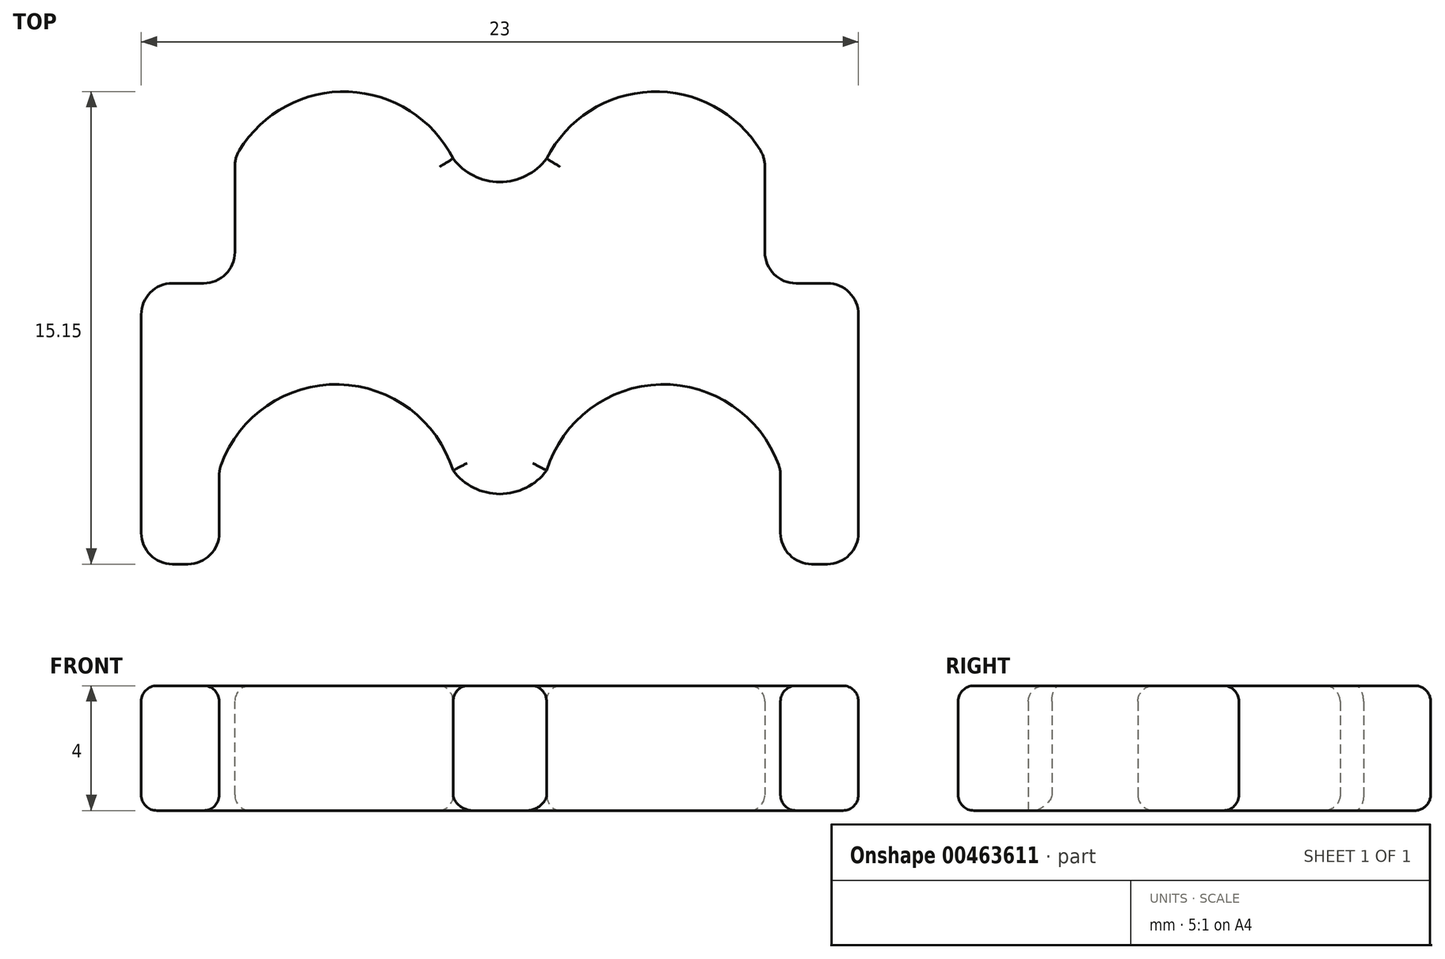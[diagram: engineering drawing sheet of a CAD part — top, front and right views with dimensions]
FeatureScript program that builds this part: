
annotation { "Feature Type Name" : "Feature", "Feature Type Description" : "" }
export const myFeature = defineFeature(function(context is Context, id is Id, definition is map)
    precondition{}
    {
        {
            var Q0;
            Q0=qCreatedBy(makeId("Top.planeOp"),FACE);
            var sketch = newSketch(context, id + "F0", { "sketchPlane" : qUnion([Q0])});
            skLineSegment(sketch, "E0", {"start": v(9, -13) * mm, "end": v(9, -10) * mm});
            skLineSegment(sketch, "E1", {"start": v(-9, -10) * mm, "end": v(-9, -13) * mm});
            skLineSegment(sketch, "E2", {"start": v(-9, -13) * mm, "end": v(-11.5, -13) * mm});
            skLineSegment(sketch, "E3", {"start": v(9, -13) * mm, "end": v(11.5, -13) * mm});
            skLineSegment(sketch, "E4", {"start": v(-11.5, -13) * mm, "end": v(-11.5, -4) * mm});
            skLineSegment(sketch, "E5", {"start": v(-11.5, -4) * mm, "end": v(-8.5, -4) * mm});
            skLineSegment(sketch, "E6", {"start": v(-8.5, -4) * mm, "end": v(-8.5, 0) * mm});
            skLineSegment(sketch, "E7", {"start": v(8.5, 0) * mm, "end": v(8.5, -4) * mm});
            skLineSegment(sketch, "E8", {"start": v(8.5, -4) * mm, "end": v(11.5, -4) * mm});
            skLineSegment(sketch, "E9", {"start": v(11.5, -4) * mm, "end": v(11.5, -13) * mm});
            skArc(sketch, "E10", {"start": v(8.5, 0) * mm, "mid": v(5, 2.15) * mm, "end": v(1.5, 0) * mm});
            skArc(sketch, "E11", {"start": v(-1.5, 0) * mm, "mid": v(0, -0.75) * mm, "end": v(1.5, 0) * mm});
            skArc(sketch, "E12", {"start": v(9, -10) * mm, "mid": v(5.25, -7.24) * mm, "end": v(1.5, -10) * mm});
            skArc(sketch, "E13", {"start": v(-1.5, -10) * mm, "mid": v(0, -10.75) * mm, "end": v(1.5, -10) * mm});
            skArc(sketch, "E14", {"start": v(-1.5, -10) * mm, "mid": v(-5.25, -7.24) * mm, "end": v(-9, -10) * mm});
            skArc(sketch, "E15", {"start": v(-1.5, 0) * mm, "mid": v(-5, 2.15) * mm, "end": v(-8.5, 0) * mm});
            skSolve(sketch);
        }
        {
            var Q0;
            Q0=makeQuery(id+"F0.imprint","IMPRINT",FACE,{"disambiguationData":[TD([[makeQuery(id+"F0.imprint","IMPRINT",EDGE,{"derivedFrom":sQuery(id+"F0.wireOp",EDGE,"E0")}),-1.0]])]});
            extrude(context, id + "F1", {"entities" : qUnion([Q0]), "depth" : 4 * mm});
        }
        {
            var Q0;
            Q0=makeQuery(id+"F1.opExtrude","SWEPT_EDGE",EDGE,{"disambiguationData":[OSD([sQuery(id+"F0.wireOp",EDGE,"JVpa2NSN-jCbz-SYZh-2br0-VPJ9OqO5sEDm"),sQuery(id+"F0.wireOp",EDGE,"TmuEh8Bb-qYGH-lmF9-es9h-PXmLGTj7apYS")])]});
            var Q1;
            Q1=makeQuery(id+"F1.opExtrude","SWEPT_EDGE",EDGE,{"disambiguationData":[OSD([sQuery(id+"F0.wireOp",EDGE,"Ta08JTOG-JjW1-DyQu-Rjfl-olB2hLuTZKrI"),sQuery(id+"F0.wireOp",EDGE,"5RLxsvr7-zWRq-nJ0O-23qe-XEgADmnkmLba")])]});
            var Q2;
            Q2=makeQuery(id+"F1.opExtrude","SWEPT_EDGE",EDGE,{"disambiguationData":[OSD([sQuery(id+"F0.wireOp",EDGE,"JVpa2NSN-jCbz-SYZh-2br0-VPJ9OqO5sEDm"),sQuery(id+"F0.wireOp",EDGE,"iIMMWLLX-5pRk-kAWc-YyXh-X3XYjQtiHgF8")])]});
            var Q3;
            Q3=makeQuery(id+"F1.opExtrude","SWEPT_EDGE",EDGE,{"disambiguationData":[OSD([sQuery(id+"F0.wireOp",EDGE,"Bp2VUUx9-f2Nf-Cqm2-FavC-f2X54JljXIIN"),sQuery(id+"F0.wireOp",EDGE,"TmuEh8Bb-qYGH-lmF9-es9h-PXmLGTj7apYS")])]});
            var Q4;
            Q4=makeQuery(id+"F1.opExtrude","SWEPT_EDGE",EDGE,{"disambiguationData":[OSD([sQuery(id+"F0.wireOp",EDGE,"aM0JYdi9-BpOH-c1Sx-eQZ7-4LdQcpM627Qa"),sQuery(id+"F0.wireOp",EDGE,"Ta08JTOG-JjW1-DyQu-Rjfl-olB2hLuTZKrI")])]});
            var Q5;
            Q5=makeQuery(id+"F1.opExtrude","SWEPT_EDGE",EDGE,{"disambiguationData":[OSD([sQuery(id+"F0.wireOp",EDGE,"5RLxsvr7-zWRq-nJ0O-23qe-XEgADmnkmLba"),sQuery(id+"F0.wireOp",EDGE,"Bp2VUUx9-f2Nf-Cqm2-FavC-f2X54JljXIIN")])]});
            var Q6;
            Q6=makeQuery(id+"F1.opExtrude","SWEPT_EDGE",EDGE,{"disambiguationData":[OSD([sQuery(id+"F0.wireOp",EDGE,"yeDMJLls-6pq1-5wso-vwFU-Q73Pk40JU32b"),sQuery(id+"F0.wireOp",EDGE,"aM0JYdi9-BpOH-c1Sx-eQZ7-4LdQcpM627Qa")])]});
            var Q7;
            Q7=makeQuery(id+"F1.opExtrude","SWEPT_EDGE",EDGE,{"disambiguationData":[OSD([sQuery(id+"F0.wireOp",EDGE,"yeDMJLls-6pq1-5wso-vwFU-Q73Pk40JU32b"),sQuery(id+"F0.wireOp",EDGE,"oADVPvip-QRiO-k2je-1GcM-0gCGYZzCVpqe")])]});
            var Q8;
            Q8=makeQuery(id+"F1.opExtrude","SWEPT_EDGE",EDGE,{"disambiguationData":[OSD([sQuery(id+"F0.wireOp",EDGE,"oADVPvip-QRiO-k2je-1GcM-0gCGYZzCVpqe"),sQuery(id+"F0.wireOp",EDGE,"10rlgXVg-n50c-kqx7-uExC-2RYqwfv1c7cX")])]});
            var Q9;
            Q9=makeQuery(id+"F1.opExtrude","SWEPT_EDGE",EDGE,{"disambiguationData":[OSD([sQuery(id+"F0.wireOp",EDGE,"TUznSBm0-cCe5-ovrQ-pSbA-vPagOil4q95r"),sQuery(id+"F0.wireOp",EDGE,"10rlgXVg-n50c-kqx7-uExC-2RYqwfv1c7cX")])]});
            var Q10;
            Q10=makeQuery(id+"F1.opExtrude","SWEPT_EDGE",EDGE,{"disambiguationData":[OSD([sQuery(id+"F0.wireOp",EDGE,"dIuJsfEi-w8Eu-UMFV-xWrQ-Q2fZL97E1xqK"),sQuery(id+"F0.wireOp",EDGE,"TUznSBm0-cCe5-ovrQ-pSbA-vPagOil4q95r")])]});
            var Q11;
            Q11=makeQuery(id+"F1.opExtrude","SWEPT_EDGE",EDGE,{"disambiguationData":[OSD([sQuery(id+"F0.wireOp",EDGE,"iIMMWLLX-5pRk-kAWc-YyXh-X3XYjQtiHgF8"),sQuery(id+"F0.wireOp",EDGE,"dIuJsfEi-w8Eu-UMFV-xWrQ-Q2fZL97E1xqK")])]});
            var Q12;
            Q12=makeQuery(id+"F1.opExtrude","SWEPT_EDGE",EDGE,{"disambiguationData":[OSD([sQuery(id+"F0.wireOp",EDGE,"yLF3BCVI-Jb2U-5dZP-aiB0-7200LCA53yiJ"),sQuery(id+"F0.wireOp",EDGE,"E2")])]});
            var Q13;
            Q13=makeQuery(id+"F1.opExtrude","SWEPT_EDGE",EDGE,{"disambiguationData":[OSD([sQuery(id+"F0.wireOp",EDGE,"E1"),sQuery(id+"F0.wireOp",EDGE,"E2")])]});
            var Q14;
            Q14=makeQuery(id+"F1.opExtrude","SWEPT_EDGE",EDGE,{"disambiguationData":[OSD([sQuery(id+"F0.wireOp",EDGE,"Zq1giByw-Wy4a-OScs-KzMb-DU4RaiEdW2Sl"),sQuery(id+"F0.wireOp",EDGE,"E1")])]});
            var Q15;
            Q15=makeQuery(id+"F1.opExtrude","SWEPT_EDGE",EDGE,{"disambiguationData":[OSD([sQuery(id+"F0.wireOp",EDGE,"E0"),sQuery(id+"F0.wireOp",EDGE,"Zq1giByw-Wy4a-OScs-KzMb-DU4RaiEdW2Sl")])]});
            var Q16;
            Q16=makeQuery(id+"F1.opExtrude","SWEPT_EDGE",EDGE,{"disambiguationData":[OSD([sQuery(id+"F0.wireOp",EDGE,"E0"),sQuery(id+"F0.wireOp",EDGE,"E3")])]});
            var Q17;
            Q17=makeQuery(id+"F1.opExtrude","SWEPT_EDGE",EDGE,{"disambiguationData":[OSD([sQuery(id+"F0.wireOp",EDGE,"W0sLsfjq-YAJu-qSV0-cM3q-n6XLMPe2tytr"),sQuery(id+"F0.wireOp",EDGE,"E3")])]});
            var Q18;
            Q18=makeQuery(id+"F1.opExtrude","SWEPT_EDGE",EDGE,{"disambiguationData":[OSD([sQuery(id+"F0.wireOp",EDGE,"E4"),sQuery(id+"F0.wireOp",EDGE,"E5")])]});
            var Q19;
            Q19=makeQuery(id+"F1.opExtrude","SWEPT_EDGE",EDGE,{"disambiguationData":[OSD([sQuery(id+"F0.wireOp",EDGE,"E5"),sQuery(id+"F0.wireOp",EDGE,"E6")])]});
            var Q20;
            Q20=makeQuery(id+"F1.opExtrude","SWEPT_EDGE",EDGE,{"disambiguationData":[OSD([sQuery(id+"F0.wireOp",EDGE,"E6"),sQuery(id+"F0.wireOp",EDGE,"37HIgoPE-k505-ApNl-kPiv-Fzmli7TXVLkK")])]});
            var Q21;
            Q21=makeQuery(id+"F1.opExtrude","SWEPT_EDGE",EDGE,{"disambiguationData":[OSD([sQuery(id+"F0.wireOp",EDGE,"37HIgoPE-k505-ApNl-kPiv-Fzmli7TXVLkK"),sQuery(id+"F0.wireOp",EDGE,"E7")])]});
            var Q22;
            Q22=makeQuery(id+"F1.opExtrude","SWEPT_EDGE",EDGE,{"disambiguationData":[OSD([sQuery(id+"F0.wireOp",EDGE,"E7"),sQuery(id+"F0.wireOp",EDGE,"E8")])]});
            var Q23;
            Q23=makeQuery(id+"F1.opExtrude","SWEPT_EDGE",EDGE,{"disambiguationData":[OSD([sQuery(id+"F0.wireOp",EDGE,"E8"),sQuery(id+"F0.wireOp",EDGE,"E9")])]});
            fillet(context, id + "F2", {"entities" : qUnion([Q0, Q1, Q2, Q3, Q4, Q5, Q6, Q7, Q8, Q9, Q10, Q11, Q12, Q13, Q14, Q15, Q16, Q17, Q18, Q19, Q20, Q21, Q22, Q23]), "radius" : 1 * mm, "tangentPropagation" : true, "allowEdgeOverflow" : false});
        }
        {
            var Q0;
            Q0=makeQuery(id+"F1.opExtrude","CAP_EDGE",EDGE,{"disambiguationData":[OSD([sQuery(id+"F0.wireOp",EDGE,"E15")])],"isStart":false});
            var Q1;
            {var subQ0=sQuery(id+"F0.wireOp",EDGE,"E15");var subQ1=sQuery(id+"F0.wireOp",EDGE,"E6");Q1=makeQuery(id+"F2.opFillet","BLEND_EDGE",EDGE,{"blendedFrom":[makeQuery(id+"F1.opExtrude","SWEPT_EDGE",EDGE,{"disambiguationData":[OSD([subQ1,subQ0])]}),makeQuery(id+"F1.opExtrude","CAP_FACE",FACE,{"disambiguationData":[OSD([sQuery(id+"F0.wireOp",EDGE,"E0"),sQuery(id+"F0.wireOp",EDGE,"E1"),sQuery(id+"F0.wireOp",EDGE,"E2"),sQuery(id+"F0.wireOp",EDGE,"E3"),sQuery(id+"F0.wireOp",EDGE,"E4"),sQuery(id+"F0.wireOp",EDGE,"E5"),subQ1,sQuery(id+"F0.wireOp",EDGE,"E7"),sQuery(id+"F0.wireOp",EDGE,"E8"),sQuery(id+"F0.wireOp",EDGE,"E9"),sQuery(id+"F0.wireOp",EDGE,"E10"),sQuery(id+"F0.wireOp",EDGE,"E11"),sQuery(id+"F0.wireOp",EDGE,"E12"),sQuery(id+"F0.wireOp",EDGE,"E13"),sQuery(id+"F0.wireOp",EDGE,"E14"),subQ0])],"isStart":false})],"blendedInto":[makeQuery(id+"F1.opExtrude","CAP_FACE",FACE,{"disambiguationData":[OSD([sQuery(id+"F0.wireOp",EDGE,"E0"),sQuery(id+"F0.wireOp",EDGE,"E1"),sQuery(id+"F0.wireOp",EDGE,"E2"),sQuery(id+"F0.wireOp",EDGE,"E3"),sQuery(id+"F0.wireOp",EDGE,"E4"),sQuery(id+"F0.wireOp",EDGE,"E5"),subQ1,sQuery(id+"F0.wireOp",EDGE,"E7"),sQuery(id+"F0.wireOp",EDGE,"E8"),sQuery(id+"F0.wireOp",EDGE,"E9"),sQuery(id+"F0.wireOp",EDGE,"E10"),sQuery(id+"F0.wireOp",EDGE,"E11"),sQuery(id+"F0.wireOp",EDGE,"E12"),sQuery(id+"F0.wireOp",EDGE,"E13"),sQuery(id+"F0.wireOp",EDGE,"E14"),subQ0])],"isStart":false})]});}
            var Q2;
            Q2=makeQuery(id+"F1.opExtrude","CAP_EDGE",EDGE,{"disambiguationData":[OSD([sQuery(id+"F0.wireOp",EDGE,"E6")])],"isStart":false});
            var Q3;
            {var subQ0=sQuery(id+"F0.wireOp",EDGE,"E6");var subQ1=sQuery(id+"F0.wireOp",EDGE,"E5");Q3=makeQuery(id+"F2.opFillet","BLEND_EDGE",EDGE,{"blendedFrom":[makeQuery(id+"F1.opExtrude","SWEPT_EDGE",EDGE,{"disambiguationData":[OSD([subQ1,subQ0])]}),makeQuery(id+"F1.opExtrude","CAP_FACE",FACE,{"disambiguationData":[OSD([sQuery(id+"F0.wireOp",EDGE,"E0"),sQuery(id+"F0.wireOp",EDGE,"E1"),sQuery(id+"F0.wireOp",EDGE,"E2"),sQuery(id+"F0.wireOp",EDGE,"E3"),sQuery(id+"F0.wireOp",EDGE,"E4"),subQ1,subQ0,sQuery(id+"F0.wireOp",EDGE,"E7"),sQuery(id+"F0.wireOp",EDGE,"E8"),sQuery(id+"F0.wireOp",EDGE,"E9"),sQuery(id+"F0.wireOp",EDGE,"E10"),sQuery(id+"F0.wireOp",EDGE,"E11"),sQuery(id+"F0.wireOp",EDGE,"E12"),sQuery(id+"F0.wireOp",EDGE,"E13"),sQuery(id+"F0.wireOp",EDGE,"E14"),sQuery(id+"F0.wireOp",EDGE,"E15")])],"isStart":false})],"blendedInto":[makeQuery(id+"F1.opExtrude","CAP_FACE",FACE,{"disambiguationData":[OSD([sQuery(id+"F0.wireOp",EDGE,"E0"),sQuery(id+"F0.wireOp",EDGE,"E1"),sQuery(id+"F0.wireOp",EDGE,"E2"),sQuery(id+"F0.wireOp",EDGE,"E3"),sQuery(id+"F0.wireOp",EDGE,"E4"),subQ1,subQ0,sQuery(id+"F0.wireOp",EDGE,"E7"),sQuery(id+"F0.wireOp",EDGE,"E8"),sQuery(id+"F0.wireOp",EDGE,"E9"),sQuery(id+"F0.wireOp",EDGE,"E10"),sQuery(id+"F0.wireOp",EDGE,"E11"),sQuery(id+"F0.wireOp",EDGE,"E12"),sQuery(id+"F0.wireOp",EDGE,"E13"),sQuery(id+"F0.wireOp",EDGE,"E14"),sQuery(id+"F0.wireOp",EDGE,"E15")])],"isStart":false})]});}
            var Q4;
            Q4=makeQuery(id+"F1.opExtrude","CAP_EDGE",EDGE,{"disambiguationData":[OSD([sQuery(id+"F0.wireOp",EDGE,"E5")])],"isStart":false});
            var Q5;
            {var subQ0=sQuery(id+"F0.wireOp",EDGE,"E5");var subQ1=sQuery(id+"F0.wireOp",EDGE,"E4");Q5=makeQuery(id+"F2.opFillet","BLEND_EDGE",EDGE,{"blendedFrom":[makeQuery(id+"F1.opExtrude","SWEPT_EDGE",EDGE,{"disambiguationData":[OSD([subQ1,subQ0])]}),makeQuery(id+"F1.opExtrude","CAP_FACE",FACE,{"disambiguationData":[OSD([sQuery(id+"F0.wireOp",EDGE,"E0"),sQuery(id+"F0.wireOp",EDGE,"E1"),sQuery(id+"F0.wireOp",EDGE,"E2"),sQuery(id+"F0.wireOp",EDGE,"E3"),subQ1,subQ0,sQuery(id+"F0.wireOp",EDGE,"E6"),sQuery(id+"F0.wireOp",EDGE,"E7"),sQuery(id+"F0.wireOp",EDGE,"E8"),sQuery(id+"F0.wireOp",EDGE,"E9"),sQuery(id+"F0.wireOp",EDGE,"E10"),sQuery(id+"F0.wireOp",EDGE,"E11"),sQuery(id+"F0.wireOp",EDGE,"E12"),sQuery(id+"F0.wireOp",EDGE,"E13"),sQuery(id+"F0.wireOp",EDGE,"E14"),sQuery(id+"F0.wireOp",EDGE,"E15")])],"isStart":false})],"blendedInto":[makeQuery(id+"F1.opExtrude","CAP_FACE",FACE,{"disambiguationData":[OSD([sQuery(id+"F0.wireOp",EDGE,"E0"),sQuery(id+"F0.wireOp",EDGE,"E1"),sQuery(id+"F0.wireOp",EDGE,"E2"),sQuery(id+"F0.wireOp",EDGE,"E3"),subQ1,subQ0,sQuery(id+"F0.wireOp",EDGE,"E6"),sQuery(id+"F0.wireOp",EDGE,"E7"),sQuery(id+"F0.wireOp",EDGE,"E8"),sQuery(id+"F0.wireOp",EDGE,"E9"),sQuery(id+"F0.wireOp",EDGE,"E10"),sQuery(id+"F0.wireOp",EDGE,"E11"),sQuery(id+"F0.wireOp",EDGE,"E12"),sQuery(id+"F0.wireOp",EDGE,"E13"),sQuery(id+"F0.wireOp",EDGE,"E14"),sQuery(id+"F0.wireOp",EDGE,"E15")])],"isStart":false})]});}
            var Q6;
            Q6=makeQuery(id+"F1.opExtrude","CAP_EDGE",EDGE,{"disambiguationData":[OSD([sQuery(id+"F0.wireOp",EDGE,"E4")])],"isStart":false});
            var Q7;
            {var subQ0=sQuery(id+"F0.wireOp",EDGE,"E4");var subQ1=sQuery(id+"F0.wireOp",EDGE,"E2");Q7=makeQuery(id+"F2.opFillet","BLEND_EDGE",EDGE,{"blendedFrom":[makeQuery(id+"F1.opExtrude","SWEPT_EDGE",EDGE,{"disambiguationData":[OSD([subQ1,subQ0])]}),makeQuery(id+"F1.opExtrude","CAP_FACE",FACE,{"disambiguationData":[OSD([sQuery(id+"F0.wireOp",EDGE,"E0"),sQuery(id+"F0.wireOp",EDGE,"E1"),subQ1,sQuery(id+"F0.wireOp",EDGE,"E3"),subQ0,sQuery(id+"F0.wireOp",EDGE,"E5"),sQuery(id+"F0.wireOp",EDGE,"E6"),sQuery(id+"F0.wireOp",EDGE,"E7"),sQuery(id+"F0.wireOp",EDGE,"E8"),sQuery(id+"F0.wireOp",EDGE,"E9"),sQuery(id+"F0.wireOp",EDGE,"E10"),sQuery(id+"F0.wireOp",EDGE,"E11"),sQuery(id+"F0.wireOp",EDGE,"E12"),sQuery(id+"F0.wireOp",EDGE,"E13"),sQuery(id+"F0.wireOp",EDGE,"E14"),sQuery(id+"F0.wireOp",EDGE,"E15")])],"isStart":false})],"blendedInto":[makeQuery(id+"F1.opExtrude","CAP_FACE",FACE,{"disambiguationData":[OSD([sQuery(id+"F0.wireOp",EDGE,"E0"),sQuery(id+"F0.wireOp",EDGE,"E1"),subQ1,sQuery(id+"F0.wireOp",EDGE,"E3"),subQ0,sQuery(id+"F0.wireOp",EDGE,"E5"),sQuery(id+"F0.wireOp",EDGE,"E6"),sQuery(id+"F0.wireOp",EDGE,"E7"),sQuery(id+"F0.wireOp",EDGE,"E8"),sQuery(id+"F0.wireOp",EDGE,"E9"),sQuery(id+"F0.wireOp",EDGE,"E10"),sQuery(id+"F0.wireOp",EDGE,"E11"),sQuery(id+"F0.wireOp",EDGE,"E12"),sQuery(id+"F0.wireOp",EDGE,"E13"),sQuery(id+"F0.wireOp",EDGE,"E14"),sQuery(id+"F0.wireOp",EDGE,"E15")])],"isStart":false})]});}
            var Q8;
            Q8=makeQuery(id+"F1.opExtrude","CAP_EDGE",EDGE,{"disambiguationData":[OSD([sQuery(id+"F0.wireOp",EDGE,"E2")])],"isStart":false});
            var Q9;
            {var subQ0=sQuery(id+"F0.wireOp",EDGE,"E2");var subQ1=sQuery(id+"F0.wireOp",EDGE,"E1");Q9=makeQuery(id+"F2.opFillet","BLEND_EDGE",EDGE,{"blendedFrom":[makeQuery(id+"F1.opExtrude","SWEPT_EDGE",EDGE,{"disambiguationData":[OSD([subQ1,subQ0])]}),makeQuery(id+"F1.opExtrude","CAP_FACE",FACE,{"disambiguationData":[OSD([sQuery(id+"F0.wireOp",EDGE,"E0"),subQ1,subQ0,sQuery(id+"F0.wireOp",EDGE,"E3"),sQuery(id+"F0.wireOp",EDGE,"E4"),sQuery(id+"F0.wireOp",EDGE,"E5"),sQuery(id+"F0.wireOp",EDGE,"E6"),sQuery(id+"F0.wireOp",EDGE,"E7"),sQuery(id+"F0.wireOp",EDGE,"E8"),sQuery(id+"F0.wireOp",EDGE,"E9"),sQuery(id+"F0.wireOp",EDGE,"E10"),sQuery(id+"F0.wireOp",EDGE,"E11"),sQuery(id+"F0.wireOp",EDGE,"E12"),sQuery(id+"F0.wireOp",EDGE,"E13"),sQuery(id+"F0.wireOp",EDGE,"E14"),sQuery(id+"F0.wireOp",EDGE,"E15")])],"isStart":false})],"blendedInto":[makeQuery(id+"F1.opExtrude","CAP_FACE",FACE,{"disambiguationData":[OSD([sQuery(id+"F0.wireOp",EDGE,"E0"),subQ1,subQ0,sQuery(id+"F0.wireOp",EDGE,"E3"),sQuery(id+"F0.wireOp",EDGE,"E4"),sQuery(id+"F0.wireOp",EDGE,"E5"),sQuery(id+"F0.wireOp",EDGE,"E6"),sQuery(id+"F0.wireOp",EDGE,"E7"),sQuery(id+"F0.wireOp",EDGE,"E8"),sQuery(id+"F0.wireOp",EDGE,"E9"),sQuery(id+"F0.wireOp",EDGE,"E10"),sQuery(id+"F0.wireOp",EDGE,"E11"),sQuery(id+"F0.wireOp",EDGE,"E12"),sQuery(id+"F0.wireOp",EDGE,"E13"),sQuery(id+"F0.wireOp",EDGE,"E14"),sQuery(id+"F0.wireOp",EDGE,"E15")])],"isStart":false})]});}
            var Q10;
            Q10=makeQuery(id+"F1.opExtrude","CAP_EDGE",EDGE,{"disambiguationData":[OSD([sQuery(id+"F0.wireOp",EDGE,"E1")])],"isStart":false});
            var Q11;
            Q11=makeQuery(id+"F1.opExtrude","CAP_EDGE",EDGE,{"disambiguationData":[OSD([sQuery(id+"F0.wireOp",EDGE,"E14")])],"isStart":false});
            var Q12;
            {var subQ0=sQuery(id+"F0.wireOp",EDGE,"E14");var subQ1=sQuery(id+"F0.wireOp",EDGE,"E1");Q12=makeQuery(id+"F2.opFillet","BLEND_EDGE",EDGE,{"blendedFrom":[makeQuery(id+"F1.opExtrude","SWEPT_EDGE",EDGE,{"disambiguationData":[OSD([subQ1,subQ0])]}),makeQuery(id+"F1.opExtrude","CAP_FACE",FACE,{"disambiguationData":[OSD([sQuery(id+"F0.wireOp",EDGE,"E0"),subQ1,sQuery(id+"F0.wireOp",EDGE,"E2"),sQuery(id+"F0.wireOp",EDGE,"E3"),sQuery(id+"F0.wireOp",EDGE,"E4"),sQuery(id+"F0.wireOp",EDGE,"E5"),sQuery(id+"F0.wireOp",EDGE,"E6"),sQuery(id+"F0.wireOp",EDGE,"E7"),sQuery(id+"F0.wireOp",EDGE,"E8"),sQuery(id+"F0.wireOp",EDGE,"E9"),sQuery(id+"F0.wireOp",EDGE,"E10"),sQuery(id+"F0.wireOp",EDGE,"E11"),sQuery(id+"F0.wireOp",EDGE,"E12"),sQuery(id+"F0.wireOp",EDGE,"E13"),subQ0,sQuery(id+"F0.wireOp",EDGE,"E15")])],"isStart":false})],"blendedInto":[makeQuery(id+"F1.opExtrude","CAP_FACE",FACE,{"disambiguationData":[OSD([sQuery(id+"F0.wireOp",EDGE,"E0"),subQ1,sQuery(id+"F0.wireOp",EDGE,"E2"),sQuery(id+"F0.wireOp",EDGE,"E3"),sQuery(id+"F0.wireOp",EDGE,"E4"),sQuery(id+"F0.wireOp",EDGE,"E5"),sQuery(id+"F0.wireOp",EDGE,"E6"),sQuery(id+"F0.wireOp",EDGE,"E7"),sQuery(id+"F0.wireOp",EDGE,"E8"),sQuery(id+"F0.wireOp",EDGE,"E9"),sQuery(id+"F0.wireOp",EDGE,"E10"),sQuery(id+"F0.wireOp",EDGE,"E11"),sQuery(id+"F0.wireOp",EDGE,"E12"),sQuery(id+"F0.wireOp",EDGE,"E13"),subQ0,sQuery(id+"F0.wireOp",EDGE,"E15")])],"isStart":false})]});}
            var Q13;
            Q13=makeQuery(id+"F1.opExtrude","CAP_EDGE",EDGE,{"disambiguationData":[OSD([sQuery(id+"F0.wireOp",EDGE,"E13")])],"isStart":false});
            var Q14;
            Q14=makeQuery(id+"F1.opExtrude","CAP_EDGE",EDGE,{"disambiguationData":[OSD([sQuery(id+"F0.wireOp",EDGE,"E12")])],"isStart":false});
            var Q15;
            {var subQ0=sQuery(id+"F0.wireOp",EDGE,"E12");var subQ1=sQuery(id+"F0.wireOp",EDGE,"E0");Q15=makeQuery(id+"F2.opFillet","BLEND_EDGE",EDGE,{"blendedFrom":[makeQuery(id+"F1.opExtrude","SWEPT_EDGE",EDGE,{"disambiguationData":[OSD([subQ1,subQ0])]}),makeQuery(id+"F1.opExtrude","CAP_FACE",FACE,{"disambiguationData":[OSD([subQ1,sQuery(id+"F0.wireOp",EDGE,"E1"),sQuery(id+"F0.wireOp",EDGE,"E2"),sQuery(id+"F0.wireOp",EDGE,"E3"),sQuery(id+"F0.wireOp",EDGE,"E4"),sQuery(id+"F0.wireOp",EDGE,"E5"),sQuery(id+"F0.wireOp",EDGE,"E6"),sQuery(id+"F0.wireOp",EDGE,"E7"),sQuery(id+"F0.wireOp",EDGE,"E8"),sQuery(id+"F0.wireOp",EDGE,"E9"),sQuery(id+"F0.wireOp",EDGE,"E10"),sQuery(id+"F0.wireOp",EDGE,"E11"),subQ0,sQuery(id+"F0.wireOp",EDGE,"E13"),sQuery(id+"F0.wireOp",EDGE,"E14"),sQuery(id+"F0.wireOp",EDGE,"E15")])],"isStart":false})],"blendedInto":[makeQuery(id+"F1.opExtrude","CAP_FACE",FACE,{"disambiguationData":[OSD([subQ1,sQuery(id+"F0.wireOp",EDGE,"E1"),sQuery(id+"F0.wireOp",EDGE,"E2"),sQuery(id+"F0.wireOp",EDGE,"E3"),sQuery(id+"F0.wireOp",EDGE,"E4"),sQuery(id+"F0.wireOp",EDGE,"E5"),sQuery(id+"F0.wireOp",EDGE,"E6"),sQuery(id+"F0.wireOp",EDGE,"E7"),sQuery(id+"F0.wireOp",EDGE,"E8"),sQuery(id+"F0.wireOp",EDGE,"E9"),sQuery(id+"F0.wireOp",EDGE,"E10"),sQuery(id+"F0.wireOp",EDGE,"E11"),subQ0,sQuery(id+"F0.wireOp",EDGE,"E13"),sQuery(id+"F0.wireOp",EDGE,"E14"),sQuery(id+"F0.wireOp",EDGE,"E15")])],"isStart":false})]});}
            var Q16;
            Q16=makeQuery(id+"F1.opExtrude","CAP_EDGE",EDGE,{"disambiguationData":[OSD([sQuery(id+"F0.wireOp",EDGE,"E0")])],"isStart":false});
            var Q17;
            {var subQ0=sQuery(id+"F0.wireOp",EDGE,"E3");var subQ1=sQuery(id+"F0.wireOp",EDGE,"E0");Q17=makeQuery(id+"F2.opFillet","BLEND_EDGE",EDGE,{"blendedFrom":[makeQuery(id+"F1.opExtrude","SWEPT_EDGE",EDGE,{"disambiguationData":[OSD([subQ1,subQ0])]}),makeQuery(id+"F1.opExtrude","CAP_FACE",FACE,{"disambiguationData":[OSD([subQ1,sQuery(id+"F0.wireOp",EDGE,"E1"),sQuery(id+"F0.wireOp",EDGE,"E2"),subQ0,sQuery(id+"F0.wireOp",EDGE,"E4"),sQuery(id+"F0.wireOp",EDGE,"E5"),sQuery(id+"F0.wireOp",EDGE,"E6"),sQuery(id+"F0.wireOp",EDGE,"E7"),sQuery(id+"F0.wireOp",EDGE,"E8"),sQuery(id+"F0.wireOp",EDGE,"E9"),sQuery(id+"F0.wireOp",EDGE,"E10"),sQuery(id+"F0.wireOp",EDGE,"E11"),sQuery(id+"F0.wireOp",EDGE,"E12"),sQuery(id+"F0.wireOp",EDGE,"E13"),sQuery(id+"F0.wireOp",EDGE,"E14"),sQuery(id+"F0.wireOp",EDGE,"E15")])],"isStart":false})],"blendedInto":[makeQuery(id+"F1.opExtrude","CAP_FACE",FACE,{"disambiguationData":[OSD([subQ1,sQuery(id+"F0.wireOp",EDGE,"E1"),sQuery(id+"F0.wireOp",EDGE,"E2"),subQ0,sQuery(id+"F0.wireOp",EDGE,"E4"),sQuery(id+"F0.wireOp",EDGE,"E5"),sQuery(id+"F0.wireOp",EDGE,"E6"),sQuery(id+"F0.wireOp",EDGE,"E7"),sQuery(id+"F0.wireOp",EDGE,"E8"),sQuery(id+"F0.wireOp",EDGE,"E9"),sQuery(id+"F0.wireOp",EDGE,"E10"),sQuery(id+"F0.wireOp",EDGE,"E11"),sQuery(id+"F0.wireOp",EDGE,"E12"),sQuery(id+"F0.wireOp",EDGE,"E13"),sQuery(id+"F0.wireOp",EDGE,"E14"),sQuery(id+"F0.wireOp",EDGE,"E15")])],"isStart":false})]});}
            var Q18;
            Q18=makeQuery(id+"F1.opExtrude","CAP_EDGE",EDGE,{"disambiguationData":[OSD([sQuery(id+"F0.wireOp",EDGE,"E3")])],"isStart":false});
            var Q19;
            {var subQ0=sQuery(id+"F0.wireOp",EDGE,"E9");var subQ1=sQuery(id+"F0.wireOp",EDGE,"E3");Q19=makeQuery(id+"F2.opFillet","BLEND_EDGE",EDGE,{"blendedFrom":[makeQuery(id+"F1.opExtrude","SWEPT_EDGE",EDGE,{"disambiguationData":[OSD([subQ1,subQ0])]}),makeQuery(id+"F1.opExtrude","CAP_FACE",FACE,{"disambiguationData":[OSD([sQuery(id+"F0.wireOp",EDGE,"E0"),sQuery(id+"F0.wireOp",EDGE,"E1"),sQuery(id+"F0.wireOp",EDGE,"E2"),subQ1,sQuery(id+"F0.wireOp",EDGE,"E4"),sQuery(id+"F0.wireOp",EDGE,"E5"),sQuery(id+"F0.wireOp",EDGE,"E6"),sQuery(id+"F0.wireOp",EDGE,"E7"),sQuery(id+"F0.wireOp",EDGE,"E8"),subQ0,sQuery(id+"F0.wireOp",EDGE,"E10"),sQuery(id+"F0.wireOp",EDGE,"E11"),sQuery(id+"F0.wireOp",EDGE,"E12"),sQuery(id+"F0.wireOp",EDGE,"E13"),sQuery(id+"F0.wireOp",EDGE,"E14"),sQuery(id+"F0.wireOp",EDGE,"E15")])],"isStart":false})],"blendedInto":[makeQuery(id+"F1.opExtrude","CAP_FACE",FACE,{"disambiguationData":[OSD([sQuery(id+"F0.wireOp",EDGE,"E0"),sQuery(id+"F0.wireOp",EDGE,"E1"),sQuery(id+"F0.wireOp",EDGE,"E2"),subQ1,sQuery(id+"F0.wireOp",EDGE,"E4"),sQuery(id+"F0.wireOp",EDGE,"E5"),sQuery(id+"F0.wireOp",EDGE,"E6"),sQuery(id+"F0.wireOp",EDGE,"E7"),sQuery(id+"F0.wireOp",EDGE,"E8"),subQ0,sQuery(id+"F0.wireOp",EDGE,"E10"),sQuery(id+"F0.wireOp",EDGE,"E11"),sQuery(id+"F0.wireOp",EDGE,"E12"),sQuery(id+"F0.wireOp",EDGE,"E13"),sQuery(id+"F0.wireOp",EDGE,"E14"),sQuery(id+"F0.wireOp",EDGE,"E15")])],"isStart":false})]});}
            var Q20;
            Q20=makeQuery(id+"F1.opExtrude","CAP_EDGE",EDGE,{"disambiguationData":[OSD([sQuery(id+"F0.wireOp",EDGE,"E9")])],"isStart":false});
            var Q21;
            Q21=makeQuery(id+"F1.opExtrude","CAP_EDGE",EDGE,{"disambiguationData":[OSD([sQuery(id+"F0.wireOp",EDGE,"E8")])],"isStart":false});
            var Q22;
            {var subQ0=sQuery(id+"F0.wireOp",EDGE,"E8");var subQ1=sQuery(id+"F0.wireOp",EDGE,"E7");Q22=makeQuery(id+"F2.opFillet","BLEND_EDGE",EDGE,{"blendedFrom":[makeQuery(id+"F1.opExtrude","SWEPT_EDGE",EDGE,{"disambiguationData":[OSD([subQ1,subQ0])]}),makeQuery(id+"F1.opExtrude","CAP_FACE",FACE,{"disambiguationData":[OSD([sQuery(id+"F0.wireOp",EDGE,"E0"),sQuery(id+"F0.wireOp",EDGE,"E1"),sQuery(id+"F0.wireOp",EDGE,"E2"),sQuery(id+"F0.wireOp",EDGE,"E3"),sQuery(id+"F0.wireOp",EDGE,"E4"),sQuery(id+"F0.wireOp",EDGE,"E5"),sQuery(id+"F0.wireOp",EDGE,"E6"),subQ1,subQ0,sQuery(id+"F0.wireOp",EDGE,"E9"),sQuery(id+"F0.wireOp",EDGE,"E10"),sQuery(id+"F0.wireOp",EDGE,"E11"),sQuery(id+"F0.wireOp",EDGE,"E12"),sQuery(id+"F0.wireOp",EDGE,"E13"),sQuery(id+"F0.wireOp",EDGE,"E14"),sQuery(id+"F0.wireOp",EDGE,"E15")])],"isStart":false})],"blendedInto":[makeQuery(id+"F1.opExtrude","CAP_FACE",FACE,{"disambiguationData":[OSD([sQuery(id+"F0.wireOp",EDGE,"E0"),sQuery(id+"F0.wireOp",EDGE,"E1"),sQuery(id+"F0.wireOp",EDGE,"E2"),sQuery(id+"F0.wireOp",EDGE,"E3"),sQuery(id+"F0.wireOp",EDGE,"E4"),sQuery(id+"F0.wireOp",EDGE,"E5"),sQuery(id+"F0.wireOp",EDGE,"E6"),subQ1,subQ0,sQuery(id+"F0.wireOp",EDGE,"E9"),sQuery(id+"F0.wireOp",EDGE,"E10"),sQuery(id+"F0.wireOp",EDGE,"E11"),sQuery(id+"F0.wireOp",EDGE,"E12"),sQuery(id+"F0.wireOp",EDGE,"E13"),sQuery(id+"F0.wireOp",EDGE,"E14"),sQuery(id+"F0.wireOp",EDGE,"E15")])],"isStart":false})]});}
            var Q23;
            {var subQ0=sQuery(id+"F0.wireOp",EDGE,"E9");var subQ1=sQuery(id+"F0.wireOp",EDGE,"E8");Q23=makeQuery(id+"F2.opFillet","BLEND_EDGE",EDGE,{"blendedFrom":[makeQuery(id+"F1.opExtrude","SWEPT_EDGE",EDGE,{"disambiguationData":[OSD([subQ1,subQ0])]}),makeQuery(id+"F1.opExtrude","CAP_FACE",FACE,{"disambiguationData":[OSD([sQuery(id+"F0.wireOp",EDGE,"E0"),sQuery(id+"F0.wireOp",EDGE,"E1"),sQuery(id+"F0.wireOp",EDGE,"E2"),sQuery(id+"F0.wireOp",EDGE,"E3"),sQuery(id+"F0.wireOp",EDGE,"E4"),sQuery(id+"F0.wireOp",EDGE,"E5"),sQuery(id+"F0.wireOp",EDGE,"E6"),sQuery(id+"F0.wireOp",EDGE,"E7"),subQ1,subQ0,sQuery(id+"F0.wireOp",EDGE,"E10"),sQuery(id+"F0.wireOp",EDGE,"E11"),sQuery(id+"F0.wireOp",EDGE,"E12"),sQuery(id+"F0.wireOp",EDGE,"E13"),sQuery(id+"F0.wireOp",EDGE,"E14"),sQuery(id+"F0.wireOp",EDGE,"E15")])],"isStart":false})],"blendedInto":[makeQuery(id+"F1.opExtrude","CAP_FACE",FACE,{"disambiguationData":[OSD([sQuery(id+"F0.wireOp",EDGE,"E0"),sQuery(id+"F0.wireOp",EDGE,"E1"),sQuery(id+"F0.wireOp",EDGE,"E2"),sQuery(id+"F0.wireOp",EDGE,"E3"),sQuery(id+"F0.wireOp",EDGE,"E4"),sQuery(id+"F0.wireOp",EDGE,"E5"),sQuery(id+"F0.wireOp",EDGE,"E6"),sQuery(id+"F0.wireOp",EDGE,"E7"),subQ1,subQ0,sQuery(id+"F0.wireOp",EDGE,"E10"),sQuery(id+"F0.wireOp",EDGE,"E11"),sQuery(id+"F0.wireOp",EDGE,"E12"),sQuery(id+"F0.wireOp",EDGE,"E13"),sQuery(id+"F0.wireOp",EDGE,"E14"),sQuery(id+"F0.wireOp",EDGE,"E15")])],"isStart":false})]});}
            var Q24;
            Q24=makeQuery(id+"F1.opExtrude","CAP_EDGE",EDGE,{"disambiguationData":[OSD([sQuery(id+"F0.wireOp",EDGE,"E7")])],"isStart":false});
            var Q25;
            {var subQ0=sQuery(id+"F0.wireOp",EDGE,"E10");var subQ1=sQuery(id+"F0.wireOp",EDGE,"E7");Q25=makeQuery(id+"F2.opFillet","BLEND_EDGE",EDGE,{"blendedFrom":[makeQuery(id+"F1.opExtrude","SWEPT_EDGE",EDGE,{"disambiguationData":[OSD([subQ1,subQ0])]}),makeQuery(id+"F1.opExtrude","CAP_FACE",FACE,{"disambiguationData":[OSD([sQuery(id+"F0.wireOp",EDGE,"E0"),sQuery(id+"F0.wireOp",EDGE,"E1"),sQuery(id+"F0.wireOp",EDGE,"E2"),sQuery(id+"F0.wireOp",EDGE,"E3"),sQuery(id+"F0.wireOp",EDGE,"E4"),sQuery(id+"F0.wireOp",EDGE,"E5"),sQuery(id+"F0.wireOp",EDGE,"E6"),subQ1,sQuery(id+"F0.wireOp",EDGE,"E8"),sQuery(id+"F0.wireOp",EDGE,"E9"),subQ0,sQuery(id+"F0.wireOp",EDGE,"E11"),sQuery(id+"F0.wireOp",EDGE,"E12"),sQuery(id+"F0.wireOp",EDGE,"E13"),sQuery(id+"F0.wireOp",EDGE,"E14"),sQuery(id+"F0.wireOp",EDGE,"E15")])],"isStart":false})],"blendedInto":[makeQuery(id+"F1.opExtrude","CAP_FACE",FACE,{"disambiguationData":[OSD([sQuery(id+"F0.wireOp",EDGE,"E0"),sQuery(id+"F0.wireOp",EDGE,"E1"),sQuery(id+"F0.wireOp",EDGE,"E2"),sQuery(id+"F0.wireOp",EDGE,"E3"),sQuery(id+"F0.wireOp",EDGE,"E4"),sQuery(id+"F0.wireOp",EDGE,"E5"),sQuery(id+"F0.wireOp",EDGE,"E6"),subQ1,sQuery(id+"F0.wireOp",EDGE,"E8"),sQuery(id+"F0.wireOp",EDGE,"E9"),subQ0,sQuery(id+"F0.wireOp",EDGE,"E11"),sQuery(id+"F0.wireOp",EDGE,"E12"),sQuery(id+"F0.wireOp",EDGE,"E13"),sQuery(id+"F0.wireOp",EDGE,"E14"),sQuery(id+"F0.wireOp",EDGE,"E15")])],"isStart":false})]});}
            var Q26;
            Q26=makeQuery(id+"F1.opExtrude","CAP_EDGE",EDGE,{"disambiguationData":[OSD([sQuery(id+"F0.wireOp",EDGE,"E10")])],"isStart":false});
            var Q27;
            Q27=makeQuery(id+"F1.opExtrude","CAP_EDGE",EDGE,{"disambiguationData":[OSD([sQuery(id+"F0.wireOp",EDGE,"E11")])],"isStart":false});
            var Q28;
            Q28=makeQuery(id+"F1.opExtrude","CAP_EDGE",EDGE,{"disambiguationData":[OSD([sQuery(id+"F0.wireOp",EDGE,"E10")])],"isStart":true});
            var Q29;
            Q29=makeQuery(id+"F1.opExtrude","CAP_EDGE",EDGE,{"disambiguationData":[OSD([sQuery(id+"F0.wireOp",EDGE,"E11")])],"isStart":true});
            var Q30;
            Q30=makeQuery(id+"F1.opExtrude","CAP_EDGE",EDGE,{"disambiguationData":[OSD([sQuery(id+"F0.wireOp",EDGE,"E15")])],"isStart":true});
            var Q31;
            {var subQ0=sQuery(id+"F0.wireOp",EDGE,"E15");var subQ1=sQuery(id+"F0.wireOp",EDGE,"E6");Q31=makeQuery(id+"F2.opFillet","BLEND_EDGE",EDGE,{"blendedFrom":[makeQuery(id+"F1.opExtrude","SWEPT_EDGE",EDGE,{"disambiguationData":[OSD([subQ1,subQ0])]}),makeQuery(id+"F1.opExtrude","CAP_FACE",FACE,{"disambiguationData":[OSD([sQuery(id+"F0.wireOp",EDGE,"E0"),sQuery(id+"F0.wireOp",EDGE,"E1"),sQuery(id+"F0.wireOp",EDGE,"E2"),sQuery(id+"F0.wireOp",EDGE,"E3"),sQuery(id+"F0.wireOp",EDGE,"E4"),sQuery(id+"F0.wireOp",EDGE,"E5"),subQ1,sQuery(id+"F0.wireOp",EDGE,"E7"),sQuery(id+"F0.wireOp",EDGE,"E8"),sQuery(id+"F0.wireOp",EDGE,"E9"),sQuery(id+"F0.wireOp",EDGE,"E10"),sQuery(id+"F0.wireOp",EDGE,"E11"),sQuery(id+"F0.wireOp",EDGE,"E12"),sQuery(id+"F0.wireOp",EDGE,"E13"),sQuery(id+"F0.wireOp",EDGE,"E14"),subQ0])],"isStart":true})],"blendedInto":[makeQuery(id+"F1.opExtrude","CAP_FACE",FACE,{"disambiguationData":[OSD([sQuery(id+"F0.wireOp",EDGE,"E0"),sQuery(id+"F0.wireOp",EDGE,"E1"),sQuery(id+"F0.wireOp",EDGE,"E2"),sQuery(id+"F0.wireOp",EDGE,"E3"),sQuery(id+"F0.wireOp",EDGE,"E4"),sQuery(id+"F0.wireOp",EDGE,"E5"),subQ1,sQuery(id+"F0.wireOp",EDGE,"E7"),sQuery(id+"F0.wireOp",EDGE,"E8"),sQuery(id+"F0.wireOp",EDGE,"E9"),sQuery(id+"F0.wireOp",EDGE,"E10"),sQuery(id+"F0.wireOp",EDGE,"E11"),sQuery(id+"F0.wireOp",EDGE,"E12"),sQuery(id+"F0.wireOp",EDGE,"E13"),sQuery(id+"F0.wireOp",EDGE,"E14"),subQ0])],"isStart":true})]});}
            var Q32;
            Q32=makeQuery(id+"F1.opExtrude","CAP_EDGE",EDGE,{"disambiguationData":[OSD([sQuery(id+"F0.wireOp",EDGE,"E6")])],"isStart":true});
            var Q33;
            {var subQ0=sQuery(id+"F0.wireOp",EDGE,"E6");var subQ1=sQuery(id+"F0.wireOp",EDGE,"E5");Q33=makeQuery(id+"F2.opFillet","BLEND_EDGE",EDGE,{"blendedFrom":[makeQuery(id+"F1.opExtrude","SWEPT_EDGE",EDGE,{"disambiguationData":[OSD([subQ1,subQ0])]}),makeQuery(id+"F1.opExtrude","CAP_FACE",FACE,{"disambiguationData":[OSD([sQuery(id+"F0.wireOp",EDGE,"E0"),sQuery(id+"F0.wireOp",EDGE,"E1"),sQuery(id+"F0.wireOp",EDGE,"E2"),sQuery(id+"F0.wireOp",EDGE,"E3"),sQuery(id+"F0.wireOp",EDGE,"E4"),subQ1,subQ0,sQuery(id+"F0.wireOp",EDGE,"E7"),sQuery(id+"F0.wireOp",EDGE,"E8"),sQuery(id+"F0.wireOp",EDGE,"E9"),sQuery(id+"F0.wireOp",EDGE,"E10"),sQuery(id+"F0.wireOp",EDGE,"E11"),sQuery(id+"F0.wireOp",EDGE,"E12"),sQuery(id+"F0.wireOp",EDGE,"E13"),sQuery(id+"F0.wireOp",EDGE,"E14"),sQuery(id+"F0.wireOp",EDGE,"E15")])],"isStart":true})],"blendedInto":[makeQuery(id+"F1.opExtrude","CAP_FACE",FACE,{"disambiguationData":[OSD([sQuery(id+"F0.wireOp",EDGE,"E0"),sQuery(id+"F0.wireOp",EDGE,"E1"),sQuery(id+"F0.wireOp",EDGE,"E2"),sQuery(id+"F0.wireOp",EDGE,"E3"),sQuery(id+"F0.wireOp",EDGE,"E4"),subQ1,subQ0,sQuery(id+"F0.wireOp",EDGE,"E7"),sQuery(id+"F0.wireOp",EDGE,"E8"),sQuery(id+"F0.wireOp",EDGE,"E9"),sQuery(id+"F0.wireOp",EDGE,"E10"),sQuery(id+"F0.wireOp",EDGE,"E11"),sQuery(id+"F0.wireOp",EDGE,"E12"),sQuery(id+"F0.wireOp",EDGE,"E13"),sQuery(id+"F0.wireOp",EDGE,"E14"),sQuery(id+"F0.wireOp",EDGE,"E15")])],"isStart":true})]});}
            var Q34;
            Q34=makeQuery(id+"F1.opExtrude","CAP_EDGE",EDGE,{"disambiguationData":[OSD([sQuery(id+"F0.wireOp",EDGE,"E5")])],"isStart":true});
            fillet(context, id + "F3", {"entities" : qUnion([Q0, Q1, Q2, Q3, Q4, Q5, Q6, Q7, Q8, Q9, Q10, Q11, Q12, Q13, Q14, Q15, Q16, Q17, Q18, Q19, Q20, Q21, Q22, Q23, Q24, Q25, Q26, Q27, Q28, Q29, Q30, Q31, Q32, Q33, Q34]), "radius" : 0.5 * mm, "tangentPropagation" : true, "allowEdgeOverflow" : false});
        }
    });
